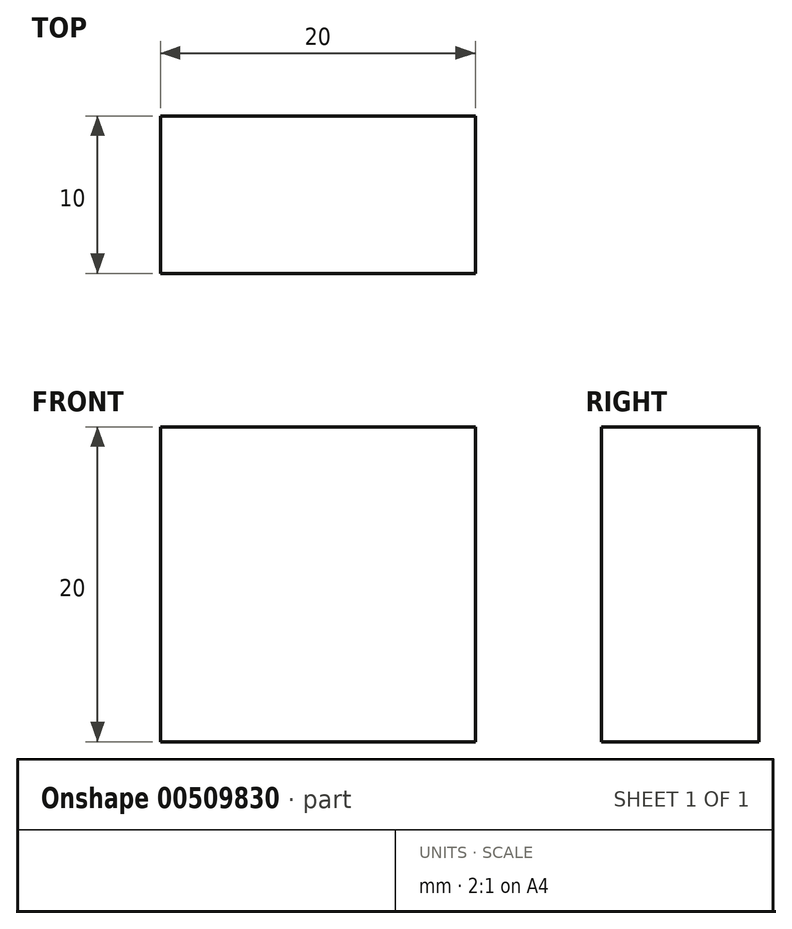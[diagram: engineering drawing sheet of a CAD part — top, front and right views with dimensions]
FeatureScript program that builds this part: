
annotation { "Feature Type Name" : "Feature", "Feature Type Description" : "" }
export const myFeature = defineFeature(function(context is Context, id is Id, definition is map)
    precondition{}
    {
        {
            var Q0;
            Q0=qCreatedBy(makeId("Front.planeOp"),FACE);
            var sketch = newSketch(context, id + "F0", { "sketchPlane" : qUnion([Q0])});
            skLineSegment(sketch, "E0.bottom", {"start": v(0, 0) * mm, "end": v(20, 0) * mm});
            skLineSegment(sketch, "E0.top", {"start": v(0, 20) * mm, "end": v(20, 20) * mm});
            skLineSegment(sketch, "E0.left", {"start": v(0, 0) * mm, "end": v(0, 20) * mm});
            skLineSegment(sketch, "E0.right", {"start": v(20, 0) * mm, "end": v(20, 20) * mm});
            skSolve(sketch);
        }
        {
            var Q0;
            Q0 = qSketchRegion(id + "F0", true);
            extrude(context, id + "F1", {"entities" : qUnion([Q0]), "depth" : 10 * mm});
        }
    });
